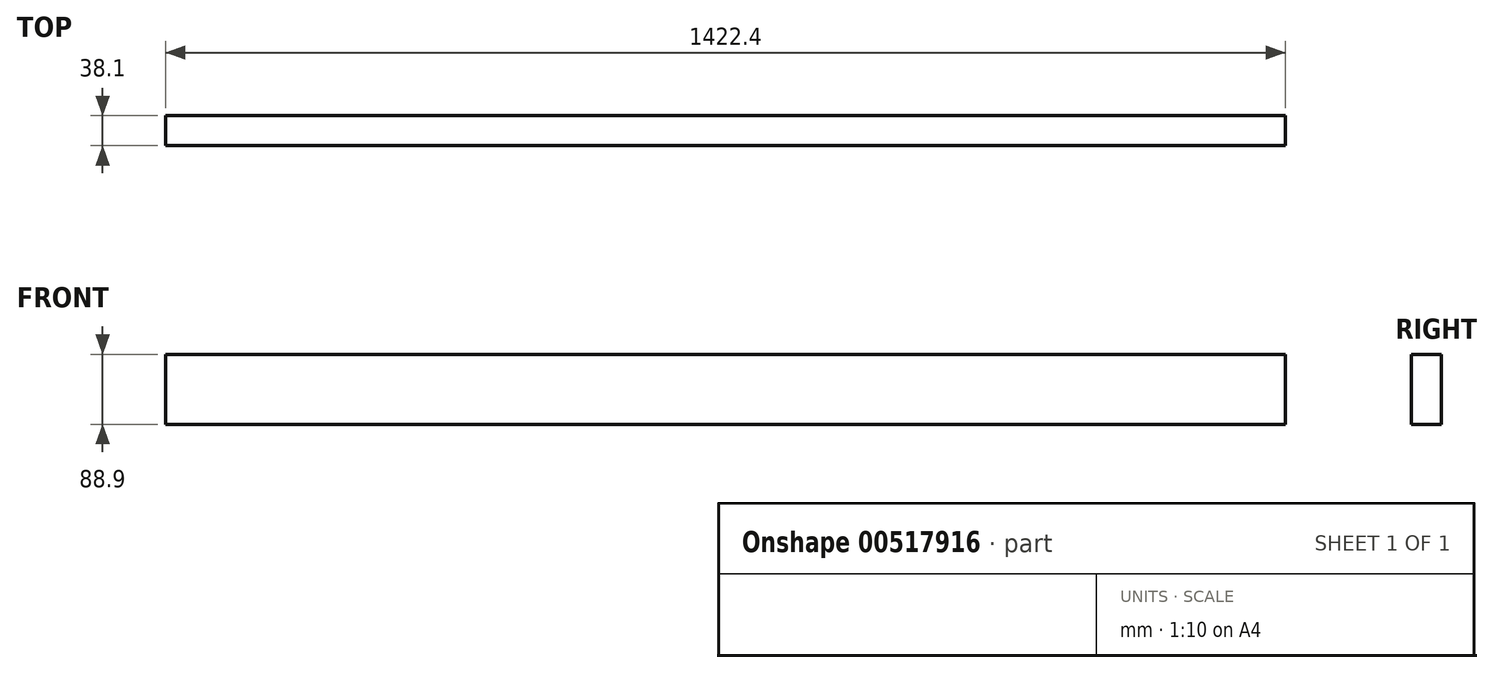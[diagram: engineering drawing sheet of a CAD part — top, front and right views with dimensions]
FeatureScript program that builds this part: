
annotation { "Feature Type Name" : "Feature", "Feature Type Description" : "" }
export const myFeature = defineFeature(function(context is Context, id is Id, definition is map)
    precondition{}
    {
        {
            var Q0;
            Q0=qCreatedBy(makeId("Right.planeOp"),FACE);
            var sketch = newSketch(context, id + "F0", { "sketchPlane" : qUnion([Q0])});
            skLineSegment(sketch, "E0.bottom", {"start": v(19.05, 44.45) * mm, "end": v(-19.05, 44.45) * mm});
            skLineSegment(sketch, "E0.top", {"start": v(19.05, -44.45) * mm, "end": v(-19.05, -44.45) * mm});
            skLineSegment(sketch, "E0.left", {"start": v(19.05, 44.45) * mm, "end": v(19.05, -44.45) * mm});
            skLineSegment(sketch, "E0.right", {"start": v(-19.05, 44.45) * mm, "end": v(-19.05, -44.45) * mm});
            skPoint(sketch, "E0.middle", {"position": v(0, 0) * mm});
            skSolve(sketch);
        }
        {
            var Q0;
            Q0=makeQuery(id+"F0.imprint","IMPRINT",FACE,{"disambiguationData":[TD([[makeQuery(id+"F0.imprint","IMPRINT",EDGE,{"derivedFrom":sQuery(id+"F0.wireOp",EDGE,"E0.bottom")}),1.0]])]});
            extrude(context, id + "F1", {"entities" : qUnion([Q0]), "endBound" : BoundingType.SYMMETRIC, "depth" : 1422.4 * mm, "offsetDistance" : 25.4 * mm});
        }
    });
